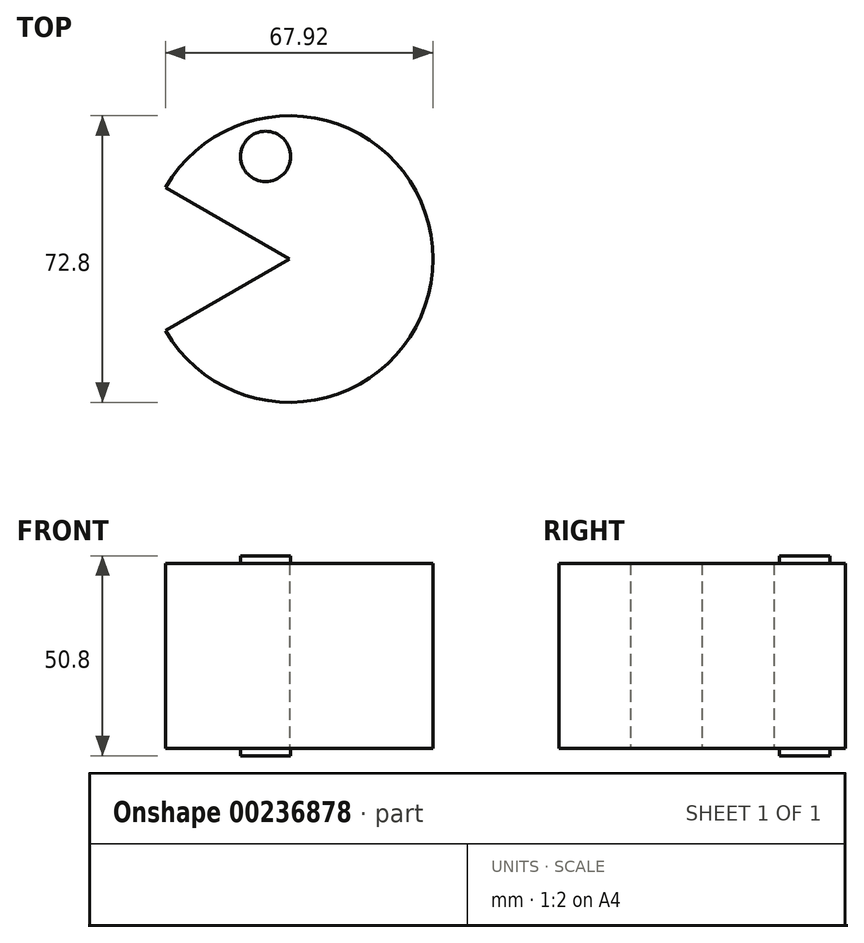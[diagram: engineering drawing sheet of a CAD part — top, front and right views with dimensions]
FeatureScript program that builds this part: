
annotation { "Feature Type Name" : "Feature", "Feature Type Description" : "" }
export const myFeature = defineFeature(function(context is Context, id is Id, definition is map)
    precondition{}
    {
        {
            var Q0;
            Q0=qCreatedBy(makeId("Front.planeOp"),FACE);
            var sketch = newSketch(context, id + "F0", { "sketchPlane" : qUnion([Q0])});
            skLineSegment(sketch, "E0.bottom", {"start": v(-36.4, 23.48) * mm, "end": v(36.4, 23.48) * mm});
            skLineSegment(sketch, "E0.top", {"start": v(-36.4, -23.48) * mm, "end": v(36.4, -23.48) * mm});
            skLineSegment(sketch, "E0.left", {"start": v(-36.4, 23.48) * mm, "end": v(-36.4, -23.48) * mm});
            skLineSegment(sketch, "E0.right", {"start": v(36.4, 23.48) * mm, "end": v(36.4, -23.48) * mm});
            skPoint(sketch, "E0.middle", {"position": v(0, 0) * mm});
            skLineSegment(sketch, "E1", {"start": v(0, 23.48) * mm, "end": v(0, -23.48) * mm});
            skSolve(sketch);
        }
        {
            var Q0;
            {var subQ0=sQuery(id+"F0.wireOp",EDGE,"E0.right");Q0=makeQuery(id+"F0.imprint","IMPRINT",FACE,{"disambiguationData":[TD([[makeQuery(id+"F0.imprint","IMPRINT",EDGE,{"derivedFrom":subQ0}),-1.0]])]});}
            var Q1;
            Q1=sQuery(id+"F0.wireOp",EDGE,"E1");
            revolve(context, id + "F1", {"entities" : qUnion([Q0]), "axis" : qUnion([Q1]), "revolveType" : RevolveType.SYMMETRIC, "angle" : 300 * degree});
        }
        {
            var Q0;
            Q0=qCreatedBy(makeId("Top.planeOp"),FACE);
            var sketch = newSketch(context, id + "F2", { "sketchPlane" : qUnion([Q0])});
            skCircle(sketch, "E2", {"center": v(-6.1, 26.07) * mm, "radius": 6.38 * mm});
            skSolve(sketch);
        }
        {
            var Q0;
            Q0 = qSketchRegion(id + "F2", true);
            extrude(context, id + "F3", {"entities" : qUnion([Q0]), "operationType" : NewBodyOperationType.ADD, "endBound" : BoundingType.SYMMETRIC, "oppositeDirection" : true, "depth" : 50.8 * mm});
        }
    });
